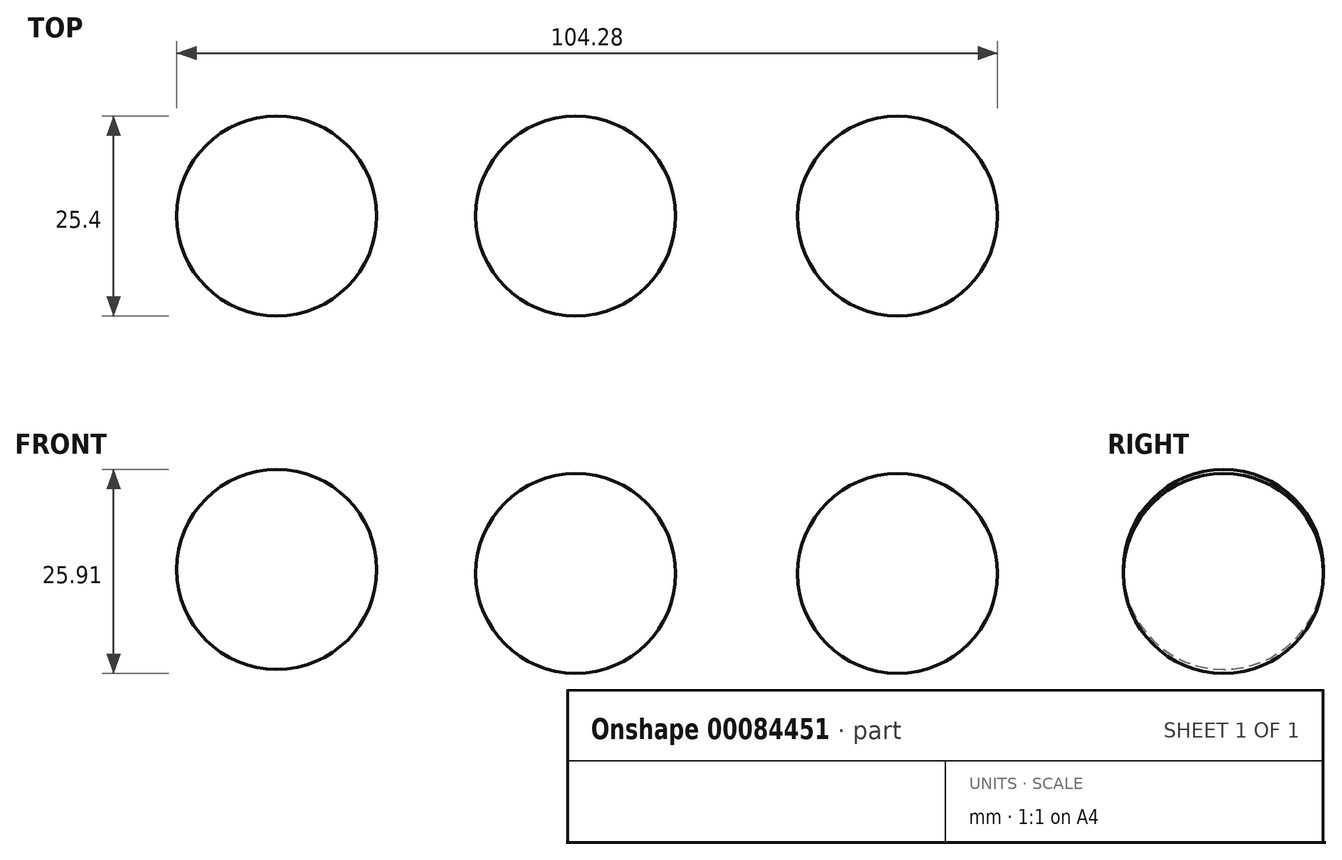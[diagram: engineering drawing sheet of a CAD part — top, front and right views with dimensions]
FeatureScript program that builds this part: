
annotation { "Feature Type Name" : "Feature", "Feature Type Description" : "" }
export const myFeature = defineFeature(function(context is Context, id is Id, definition is map)
    precondition{}
    {
        {
            var Q0;
            Q0=qCreatedBy(makeId("Front.planeOp"),FACE);
            var sketch = newSketch(context, id + "F0", { "sketchPlane" : qUnion([Q0])});
            skCircle(sketch, "E0", {"center": v(0, 0) * mm, "radius": 12.7 * mm});
            skCircle(sketch, "E1.MirrorC", {"center": v(-37.99, 0.5) * mm, "radius": 12.7 * mm});
            skCircle(sketch, "E2.MirrorC", {"center": v(40.9, 0) * mm, "radius": 12.7 * mm});
            skSolve(sketch);
        }
        {
            var Q0;
            Q0 = qSketchRegion(id + "F0", true);
            extrude(context, id + "F1", {"entities" : qUnion([Q0]), "depth" : 25.4 * mm});
        }
        {
            var Q0;
            Q0=makeQuery(id+"F1.opExtrude","CAP_EDGE",EDGE,{"disambiguationData":[OSD([sQuery(id+"F0.wireOp",EDGE,"E0")])],"isStart":true});
            var Q1;
            Q1=makeQuery(id+"F1.opExtrude","CAP_EDGE",EDGE,{"disambiguationData":[OSD([sQuery(id+"F0.wireOp",EDGE,"E0")])],"isStart":false});
            fillet(context, id + "F2", {"entities" : qUnion([Q0, Q1]), "radius" : 12.7 * mm, "tangentPropagation" : true, "allowEdgeOverflow" : false});
        }
        {
            var Q0;
            Q0=makeQuery(id+"F1.opExtrude","CAP_EDGE",EDGE,{"disambiguationData":[OSD([sQuery(id+"F0.wireOp",EDGE,"E1.MirrorC")])],"isStart":false});
            var Q1;
            Q1=makeQuery(id+"F1.opExtrude","CAP_EDGE",EDGE,{"disambiguationData":[OSD([sQuery(id+"F0.wireOp",EDGE,"E1.MirrorC")])],"isStart":true});
            fillet(context, id + "F3", {"entities" : qUnion([Q0, Q1]), "radius" : 12.7 * mm, "tangentPropagation" : true, "allowEdgeOverflow" : false});
        }
        {
            var Q0;
            Q0=makeQuery(id+"F1.opExtrude","CAP_EDGE",EDGE,{"disambiguationData":[OSD([sQuery(id+"F0.wireOp",EDGE,"E2.MirrorC")])],"isStart":false});
            var Q1;
            Q1=makeQuery(id+"F1.opExtrude","CAP_EDGE",EDGE,{"disambiguationData":[OSD([sQuery(id+"F0.wireOp",EDGE,"E2.MirrorC")])],"isStart":true});
            fillet(context, id + "F4", {"entities" : qUnion([Q0, Q1]), "radius" : 12.7 * mm, "tangentPropagation" : true, "allowEdgeOverflow" : false});
        }
    });
